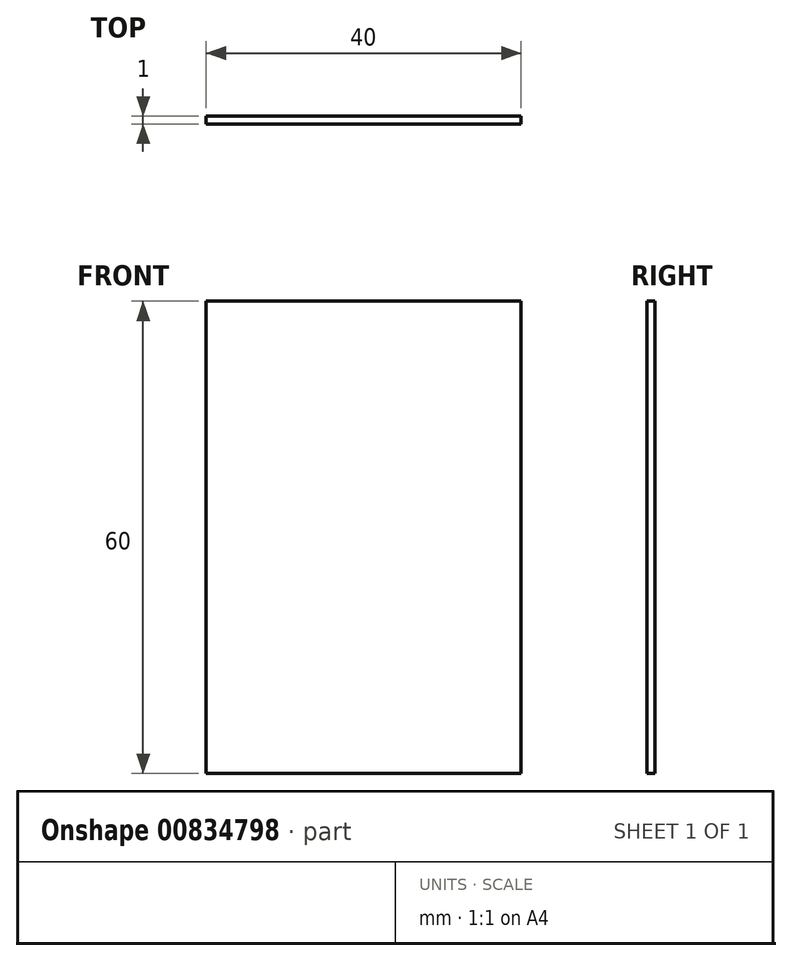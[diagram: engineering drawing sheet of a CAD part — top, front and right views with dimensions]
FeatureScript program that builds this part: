
annotation { "Feature Type Name" : "Feature", "Feature Type Description" : "" }
export const myFeature = defineFeature(function(context is Context, id is Id, definition is map)
    precondition{}
    {
        {
            var Q0;
            Q0=qCreatedBy(makeId("Front.planeOp"),FACE);
            var sketch = newSketch(context, id + "F0", { "sketchPlane" : qUnion([Q0])});
            skLineSegment(sketch, "E0.bottom", {"start": v(20, 30) * mm, "end": v(-20, 30) * mm});
            skLineSegment(sketch, "E0.top", {"start": v(20, -30) * mm, "end": v(-20, -30) * mm});
            skLineSegment(sketch, "E0.left", {"start": v(20, 30) * mm, "end": v(20, -30) * mm});
            skLineSegment(sketch, "E0.right", {"start": v(-20, 30) * mm, "end": v(-20, -30) * mm});
            skPoint(sketch, "E0.middle", {"position": v(0, 0) * mm});
            skSolve(sketch);
        }
        {
            var Q0;
            Q0 = qSketchRegion(id + "F0", true);
            extrude(context, id + "F1", {"entities" : qUnion([Q0]), "depth" : 1 * mm, "offsetDistance" : 25 * mm});
        }
    });
